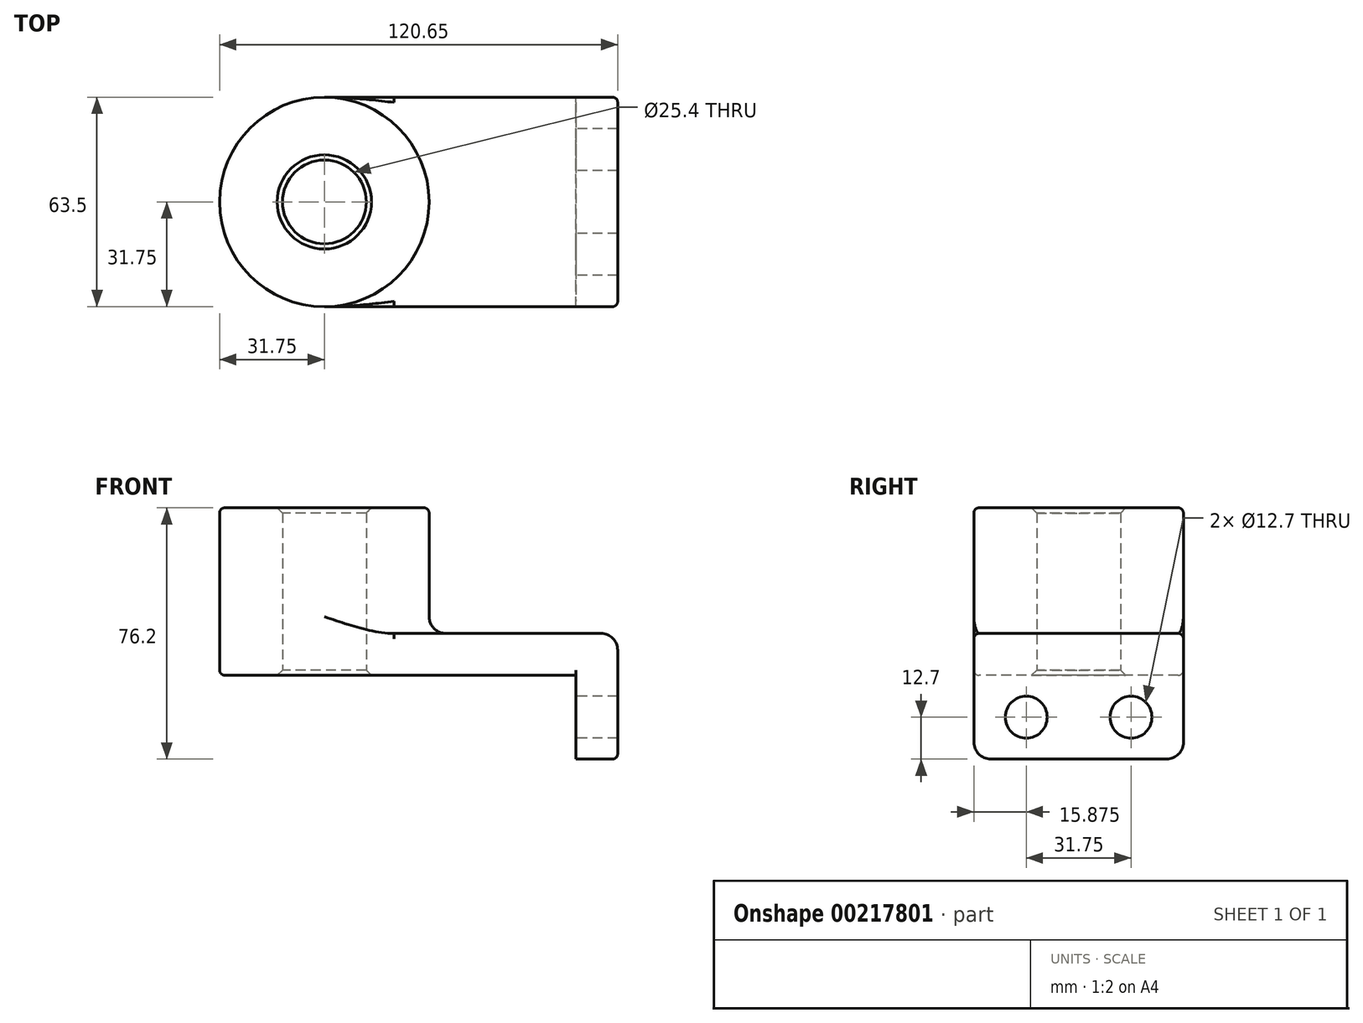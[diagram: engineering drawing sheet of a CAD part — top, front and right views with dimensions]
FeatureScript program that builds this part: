
annotation { "Feature Type Name" : "Feature", "Feature Type Description" : "" }
export const myFeature = defineFeature(function(context is Context, id is Id, definition is map)
    precondition{}
    {
        {
            var Q0;
            Q0=qCreatedBy(makeId("Top.planeOp"),FACE);
            var sketch = newSketch(context, id + "F0", { "sketchPlane" : qUnion([Q0])});
            skLineSegment(sketch, "E0.bottom", {"start": v(38.1, 31.75) * mm, "end": v(-38.1, 31.75) * mm});
            skLineSegment(sketch, "E0.top", {"start": v(38.1, -31.75) * mm, "end": v(-38.1, -31.75) * mm});
            skLineSegment(sketch, "E0.left", {"start": v(38.1, 31.75) * mm, "end": v(38.1, -31.75) * mm});
            skLineSegment(sketch, "E0.right", {"start": v(-38.1, 31.75) * mm, "end": v(-38.1, -31.75) * mm});
            skPoint(sketch, "E0.middle", {"position": v(0, 0) * mm});
            skCircle(sketch, "E1", {"center": v(-38.1, 0) * mm, "radius": 31.75 * mm});
            skCircle(sketch, "E2", {"center": v(-38.1, 0) * mm, "radius": 12.7 * mm});
            skSolve(sketch);
        }
        {
            var Q0;
            {var subQ1=sQuery(id+"F0.wireOp",EDGE,"E0.right");var subQ3=sQuery(id+"F0.wireOp",EDGE,"E2");var subQ4=makeQuery(id+"F0.imprint","INTERSECT",VERTEX,{"disambiguationData":[OD(0.0)],"derivedFrom":[subQ1,subQ3]});Q0=makeQuery(id+"F0.imprint","IMPRINT",FACE,{"disambiguationData":[TD([[makeQuery(id+"F0.imprint","IMPRINT",EDGE,{"disambiguationData":[TD([[subQ4,1.0]])],"derivedFrom":subQ3}),-1.0]])]});}
            var Q1;
            {var subQ1=sQuery(id+"F0.wireOp",EDGE,"E0.right");var subQ3=sQuery(id+"F0.wireOp",EDGE,"E2");var subQ4=makeQuery(id+"F0.imprint","INTERSECT",VERTEX,{"disambiguationData":[OD(0.0)],"derivedFrom":[subQ1,subQ3]});Q1=makeQuery(id+"F0.imprint","IMPRINT",FACE,{"disambiguationData":[TD([[makeQuery(id+"F0.imprint","IMPRINT",EDGE,{"disambiguationData":[TD([[subQ4,-1.0]])],"derivedFrom":subQ3}),-1.0]])]});}
            var Q2;
            {var subQ0=sQuery(id+"F0.wireOp",EDGE,"E0.bottom");Q2=makeQuery(id+"F0.imprint","IMPRINT",FACE,{"disambiguationData":[TD([[makeQuery(id+"F0.imprint","IMPRINT",EDGE,{"derivedFrom":subQ0}),1.0]])]});}
            extrude(context, id + "F1", {"entities" : qUnion([Q0, Q1, Q2]), "depth" : 12.7 * mm});
        }
        {
            var Q0;
            {var subQ1=sQuery(id+"F0.wireOp",EDGE,"E0.right");var subQ3=sQuery(id+"F0.wireOp",EDGE,"E2");var subQ4=makeQuery(id+"F0.imprint","INTERSECT",VERTEX,{"disambiguationData":[OD(0.0)],"derivedFrom":[subQ1,subQ3]});Q0=makeQuery(id+"F0.imprint","IMPRINT",FACE,{"disambiguationData":[TD([[makeQuery(id+"F0.imprint","IMPRINT",EDGE,{"disambiguationData":[TD([[subQ4,1.0]])],"derivedFrom":subQ3}),-1.0]])]});}
            var Q1;
            {var subQ1=sQuery(id+"F0.wireOp",EDGE,"E0.right");var subQ3=sQuery(id+"F0.wireOp",EDGE,"E2");var subQ4=makeQuery(id+"F0.imprint","INTERSECT",VERTEX,{"disambiguationData":[OD(0.0)],"derivedFrom":[subQ1,subQ3]});Q1=makeQuery(id+"F0.imprint","IMPRINT",FACE,{"disambiguationData":[TD([[makeQuery(id+"F0.imprint","IMPRINT",EDGE,{"disambiguationData":[TD([[subQ4,-1.0]])],"derivedFrom":subQ3}),-1.0]])]});}
            extrude(context, id + "F2", {"entities" : qUnion([Q0, Q1]), "operationType" : NewBodyOperationType.ADD, "depth" : 50.8 * mm});
        }
        {
            var Q0;
            Q0=makeQuery(id+"F1.opExtrude","SWEPT_FACE",FACE,{"disambiguationData":[OSD([sQuery(id+"F0.wireOp",EDGE,"E0.left")])]});
            var sketch = newSketch(context, id + "F3", { "sketchPlane" : qUnion([Q0])});
            skLineSegment(sketch, "E3.bottom", {"start": v(-31.75, 12.7) * mm, "end": v(31.75, 12.7) * mm});
            skLineSegment(sketch, "E3.top", {"start": v(-31.75, -25.4) * mm, "end": v(31.75, -25.4) * mm});
            skLineSegment(sketch, "E3.left", {"start": v(-31.75, 12.7) * mm, "end": v(-31.75, -25.4) * mm});
            skLineSegment(sketch, "E3.right", {"start": v(31.75, 12.7) * mm, "end": v(31.75, -25.4) * mm});
            skLineSegment(sketch, "E4", {"start": v(0, -25.4) * mm, "end": v(0, 0) * mm});
            skCircle(sketch, "E5", {"center": v(-15.87, -12.7) * mm, "radius": 6.35 * mm});
            skLineSegment(sketch, "E6.MirrorCS", {"start": v(0, -18.52) * mm, "end": v(0, 0) * mm});
            skCircle(sketch, "E7.MirrorC", {"center": v(15.88, -12.7) * mm, "radius": 6.35 * mm});
            skSolve(sketch);
        }
        {
            var Q0;
            Q0 = qSketchRegion(id + "F3", true);
            extrude(context, id + "F4", {"entities" : qUnion([Q0]), "operationType" : NewBodyOperationType.ADD, "depth" : 12.7 * mm});
        }
        {
            var Q0;
            {var subQ0=sQuery(id+"F0.wireOp",EDGE,"E1");Q0=makeQuery(id+"F2.boolean.opBoolean","INTERSECT",EDGE,{"derivedFrom":[makeQuery(id+"F1.opExtrude","CAP_FACE",FACE,{"disambiguationData":[OSD([sQuery(id+"F0.wireOp",EDGE,"E0.bottom"),sQuery(id+"F0.wireOp",EDGE,"E0.top"),sQuery(id+"F0.wireOp",EDGE,"E0.left"),subQ0,sQuery(id+"F0.wireOp",EDGE,"E2")])],"isStart":false}),makeQuery(id+"F2.opExtrude","SWEPT_FACE",FACE,{"disambiguationData":[OSD([subQ0])]})]});}
            var Q1;
            Q1=makeQuery(id+"F4.opExtrude","SWEPT_EDGE",EDGE,{"disambiguationData":[OSD([sQuery(id+"F3.wireOp",EDGE,"E3.top"),sQuery(id+"F3.wireOp",EDGE,"E3.left")])]});
            var Q2;
            Q2=makeQuery(id+"F4.opExtrude","SWEPT_EDGE",EDGE,{"disambiguationData":[OSD([sQuery(id+"F3.wireOp",EDGE,"E3.top"),sQuery(id+"F3.wireOp",EDGE,"E3.right")])]});
            var Q3;
            Q3=makeQuery(id+"F4.opExtrude","CAP_EDGE",EDGE,{"disambiguationData":[OSD([sQuery(id+"F3.wireOp",EDGE,"E3.bottom")])],"isStart":false});
            var Q4;
            Q4=makeQuery(id+"F1.opExtrude","CAP_EDGE",EDGE,{"disambiguationData":[OSD([sQuery(id+"F0.wireOp",EDGE,"E0.left")])],"isStart":true});
            fillet(context, id + "F5", {"entities" : qUnion([Q0, Q1, Q2, Q3, Q4]), "radius" : 5.08 * mm, "tangentPropagation" : true, "allowEdgeOverflow" : false});
        }
        {
            var Q0;
            Q0=makeQuery(id+"F4.boolean.opBoolean","MERGE",EDGE,{"derivedFrom":[makeQuery(id+"F1.opExtrude","CAP_EDGE",EDGE,{"disambiguationData":[OSD([sQuery(id+"F0.wireOp",EDGE,"E0.top")])],"isStart":false}),makeQuery(id+"F4.opExtrude","SWEPT_EDGE",EDGE,{"disambiguationData":[OSD([sQuery(id+"F3.wireOp",EDGE,"E3.bottom"),sQuery(id+"F3.wireOp",EDGE,"E3.left")])]})]});
            var Q1;
            Q1=makeQuery(id+"F1.opExtrude","CAP_EDGE",EDGE,{"disambiguationData":[OSD([sQuery(id+"F0.wireOp",EDGE,"E0.top")])],"isStart":true});
            var Q2;
            Q2=makeQuery(id+"F2.opExtrude","CAP_EDGE",EDGE,{"disambiguationData":[OSD([sQuery(id+"F0.wireOp",EDGE,"E1")])],"isStart":false});
            fillet(context, id + "F6", {"entities" : qUnion([Q0, Q1, Q2]), "radius" : 1.59 * mm, "tangentPropagation" : true, "allowEdgeOverflow" : false});
        }
        {
            var Q0;
            {var subQ0=sQuery(id+"F0.wireOp",EDGE,"E2");Q0=makeQuery(id+"F2.boolean.opBoolean","MERGE",FACE,{"derivedFrom":[makeQuery(id+"F1.opExtrude","SWEPT_FACE",FACE,{"disambiguationData":[OSD([subQ0])]}),makeQuery(id+"F2.opExtrude","SWEPT_FACE",FACE,{"disambiguationData":[OSD([subQ0])]})]});}
            chamfer(context, id + "F7", {"entities" : qUnion([Q0]), "width" : 1.59 * mm, "tangentPropagation" : true});
        }
    });
